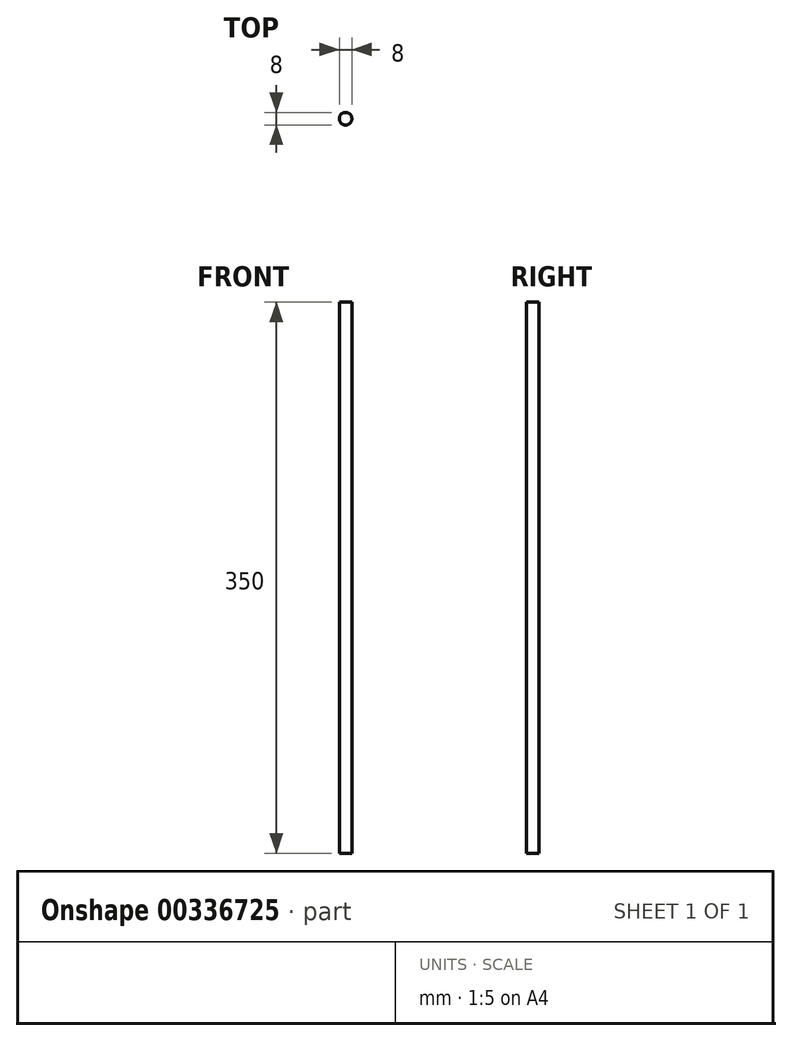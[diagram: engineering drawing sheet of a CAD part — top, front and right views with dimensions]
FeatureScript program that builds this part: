
annotation { "Feature Type Name" : "Feature", "Feature Type Description" : "" }
export const myFeature = defineFeature(function(context is Context, id is Id, definition is map)
    precondition{}
    {
        {
            var Q0;
            Q0=qCreatedBy(makeId("Top.planeOp"),FACE);
            var sketch = newSketch(context, id + "F0", { "sketchPlane" : qUnion([Q0])});
            skCircle(sketch, "E0", {"center": v(0, 0) * mm, "radius": 4 * mm});
            skSolve(sketch);
        }
        {
            var Q0;
            Q0=makeQuery(id+"F0.imprint","IMPRINT",FACE,{"disambiguationData":[TD([[makeQuery(id+"F0.imprint","IMPRINT",EDGE,{"derivedFrom":sQuery(id+"F0.wireOp",EDGE,"E0")}),1.0]])]});
            extrude(context, id + "F1", {"entities" : qUnion([Q0]), "depth" : 350 * mm});
        }
    });
